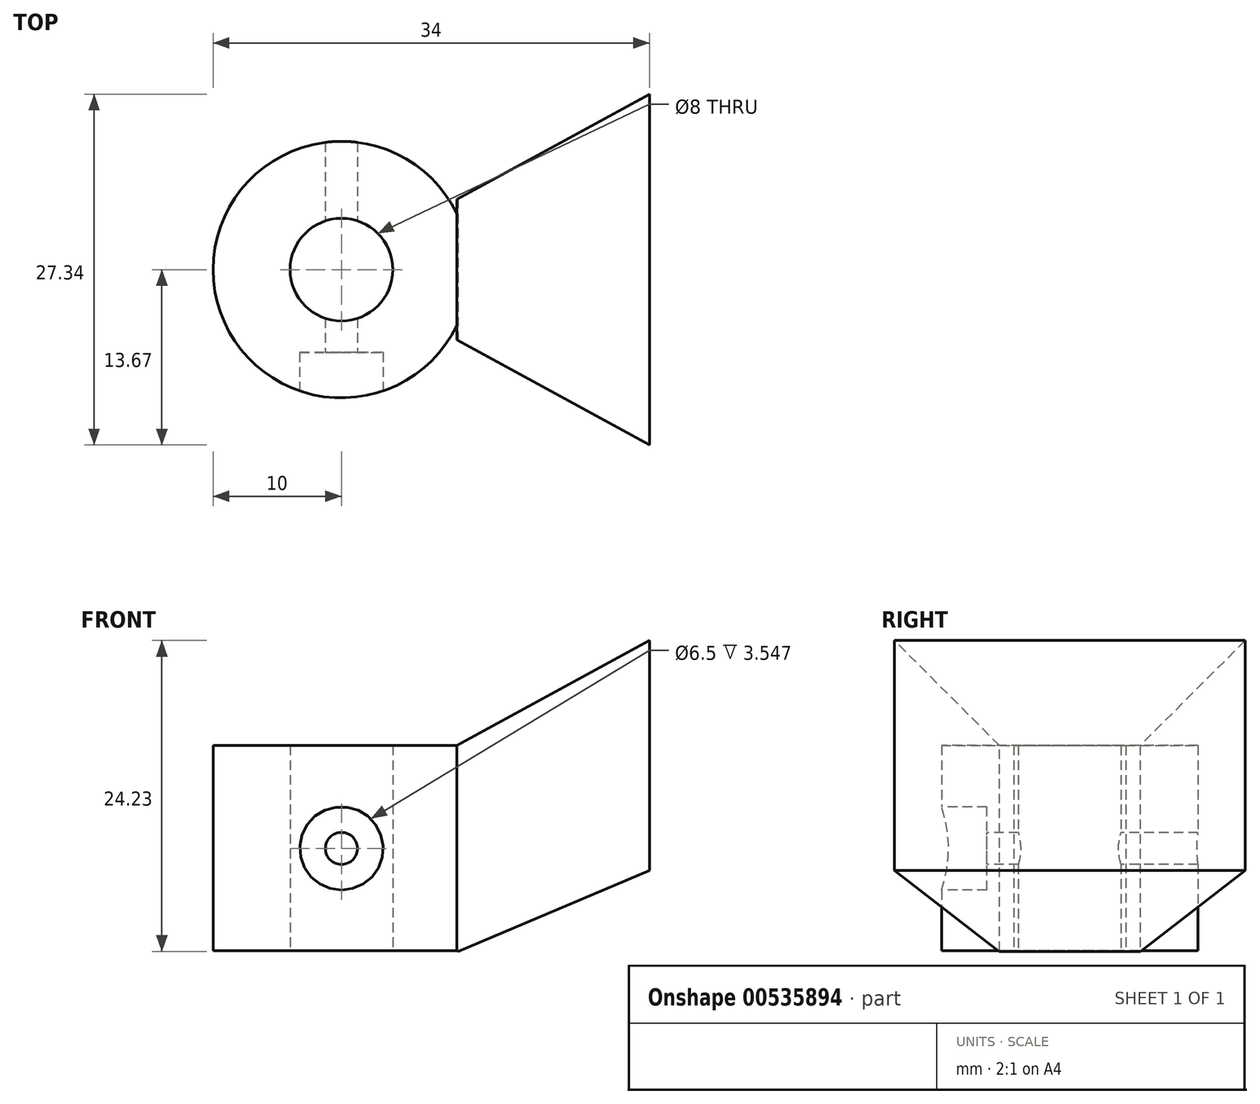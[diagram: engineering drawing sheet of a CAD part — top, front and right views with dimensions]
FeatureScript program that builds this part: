
annotation { "Feature Type Name" : "Feature", "Feature Type Description" : "" }
export const myFeature = defineFeature(function(context is Context, id is Id, definition is map)
    precondition{}
    {
        {
            var Q0;
            Q0=qCreatedBy(makeId("Top.planeOp"),FACE);
            var sketch = newSketch(context, id + "F0", { "sketchPlane" : qUnion([Q0])});
            skCircle(sketch, "E0", {"center": v(0, 0) * mm, "radius": 4 * mm});
            skCircle(sketch, "E1", {"center": v(0, 0) * mm, "radius": 10 * mm});
            skSolve(sketch);
        }
        {
            var Q0;
            Q0=makeQuery(id+"F0.imprint","IMPRINT",FACE,{"disambiguationData":[TD([[makeQuery(id+"F0.imprint","IMPRINT",EDGE,{"derivedFrom":sQuery(id+"F0.wireOp",EDGE,"E0")}),-1.0]])]});
            extrude(context, id + "F1", {"entities" : qUnion([Q0]), "depth" : 16 * mm, "offsetDistance" : 25 * mm});
        }
        {
            var Q0;
            Q0=qCreatedBy(makeId("Front.planeOp"),FACE);
            cPlane(context, id + "F2", {"entities" : qUnion([Q0]), "cplaneType" : CPlaneType.OFFSET, "offset" : 10 * mm, "width" : 150 * mm, "height" : 150 * mm});
        }
        {
            var Q0;
            Q0=qCreatedBy(id+"F2.planeOp",FACE);
            var sketch = newSketch(context, id + "F3", { "sketchPlane" : qUnion([Q0])});
            skLineSegment(sketch, "E2", {"start": v(0, 0) * mm, "end": v(0, 15.97) * mm, "construction": true});
            skCircle(sketch, "E3", {"center": v(0, 7.98) * mm, "radius": 1.75 * mm});
            skSolve(sketch);
        }
        {
            var Q0;
            Q0=sQuery(id+"F3.wireOp",VERTEX,"E3.center");
            var Q1;
            Q1=makeQuery(id+"F1.opExtrude","SWEPT_BODY",BODY,{"disambiguationData":[OSD([sQuery(id+"F0.wireOp",EDGE,"E0"),sQuery(id+"F0.wireOp",EDGE,"E1")])]});
            hole(context, id + "F4", {"style" : HoleStyle.C_BORE, "endStyle" : HoleEndStyle.THROUGH, "standardTappedOrClearance" : lookupTablePath({ "standard" : "ISO", "fit" : "Normal", "engagement" : "75%", "pitch" : "0.5 mm", "size" : "M3", "type" : "Tapped" }), "standardBlindInLast" : lookupTablePath({ "fit" : "Standard", "standard" : "ISO", "engagement" : "75%", "pitch" : "0.5 mm", "size" : "M3", "type" : "Tapped" }), "holeDiameter" : 2.5 * mm, "cBoreDiameter" : 6.5 * mm, "cBoreDepth" : 3 * mm, "majorDiameter" : 3 * mm, "showTappedDepth" : true, "isTappedThrough" : true, "tappedDepth" : 12 * mm, "tapClearance" : 3, "locations" : qUnion([Q0]), "scope" : qUnion([Q1])});
        }
        {
            var Q0;
            Q0=qCreatedBy(makeId("Right.planeOp"),FACE);
            cPlane(context, id + "F5", {"entities" : qUnion([Q0]), "cplaneType" : CPlaneType.OFFSET, "offset" : 9 * mm, "width" : 150 * mm, "height" : 150 * mm});
        }
        {
            var Q0;
            Q0=qCreatedBy(id+"F5.planeOp",FACE);
            var sketch = newSketch(context, id + "F6", { "sketchPlane" : qUnion([Q0])});
            skLineSegment(sketch, "E4.0", {"start": v(-10, 16) * mm, "end": v(10, 16) * mm, "construction": true});
            skLineSegment(sketch, "E5.0", {"start": v(-10, 0) * mm, "end": v(10, 0) * mm, "construction": true});
            skLineSegment(sketch, "E6", {"start": v(0, 16) * mm, "end": v(0, 0) * mm, "construction": true});
            skLineSegment(sketch, "E7.bottom", {"start": v(5.47, 0) * mm, "end": v(-5.47, 0) * mm});
            skLineSegment(sketch, "E7.top", {"start": v(5.47, 16) * mm, "end": v(-5.47, 16) * mm});
            skLineSegment(sketch, "E7.left", {"start": v(5.47, 0) * mm, "end": v(5.47, 16) * mm});
            skLineSegment(sketch, "E7.right", {"start": v(-5.47, 0) * mm, "end": v(-5.47, 16) * mm});
            skPoint(sketch, "E7.middle", {"position": v(0, 8) * mm});
            skSolve(sketch);
        }
        {
            var Q0;
            Q0=makeQuery(id+"F6.imprint","IMPRINT",FACE,{"disambiguationData":[TD([[makeQuery(id+"F6.imprint","IMPRINT",EDGE,{"derivedFrom":sQuery(id+"F6.wireOp",EDGE,"E7.bottom")}),-1.0]])]});
            extrude(context, id + "F7", {"entities" : qUnion([Q0]), "operationType" : NewBodyOperationType.ADD, "depth" : 15 * mm, "offsetDistance" : 25 * mm, "hasDraft" : true, "draftAngle" : 0.5 * radian});
        }
        {
            var Q0;
            Q0=makeQuery(id+"F7.opExtrude","CAP_EDGE",EDGE,{"disambiguationData":[OSD([sQuery(id+"F6.wireOp",EDGE,"E7.bottom")])],"isStart":false});
            chamfer(context, id + "F8", {"entities" : qUnion([Q0]), "chamferType" : ChamferType.OFFSET_ANGLE, "width" : 17 * mm, "oppositeDirection" : false, "angle" : .9 * radian, "tangentPropagation" : true});
        }
    });
